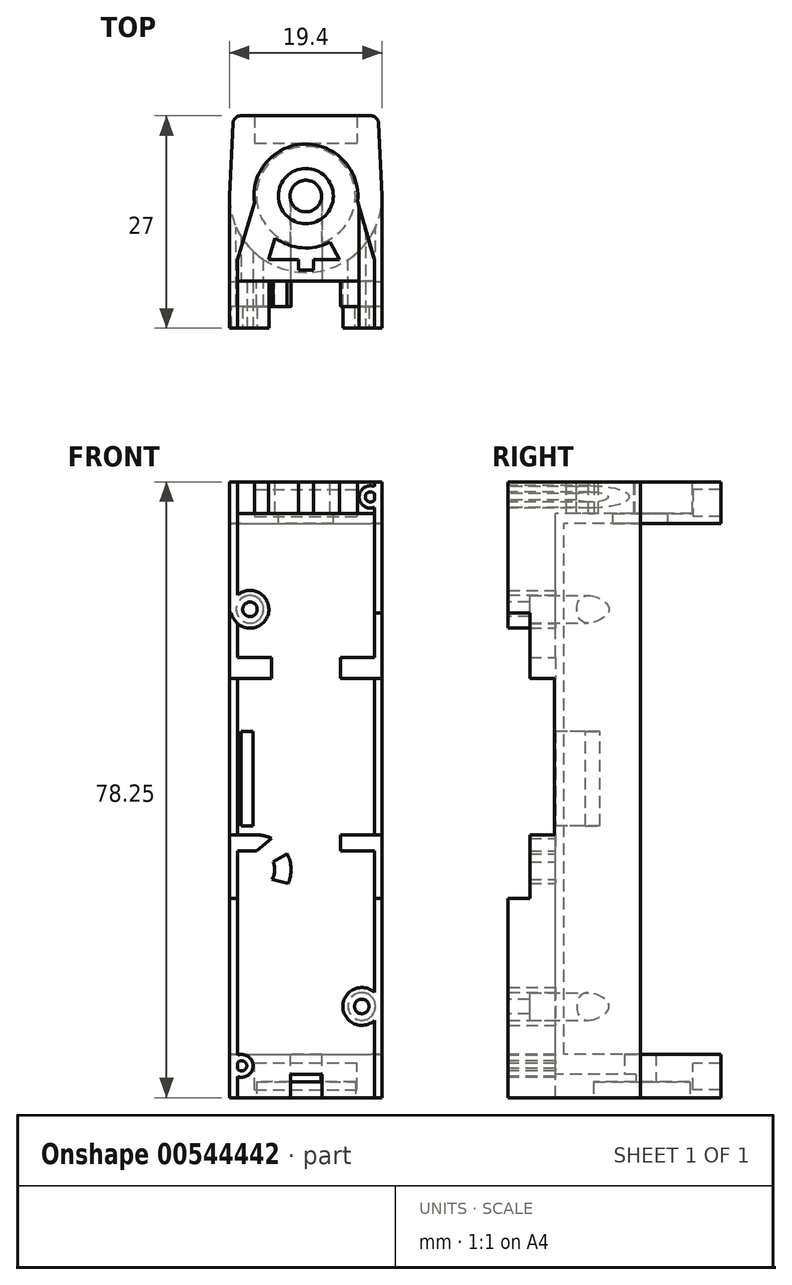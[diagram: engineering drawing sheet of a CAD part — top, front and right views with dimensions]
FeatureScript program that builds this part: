
annotation { "Feature Type Name" : "Feature", "Feature Type Description" : "" }
export const myFeature = defineFeature(function(context is Context, id is Id, definition is map)
    precondition{}
    {
        {
            var Q0;
            Q0=qCreatedBy(makeId("Top.planeOp"),FACE);
            var Q1;
            Q1=qBodyType(qCreatedBy(id+"F3",EDGE),BodyType.WIRE);
            cPlane(context, id + "F0", {"entities" : qUnion([Q0, Q1]), "cplaneType" : CPlaneType.OFFSET, "offset" : 39.25 * mm, "width" : 150 * mm, "height" : 150 * mm});
        }
        {
            var Q0;
            Q0=qCreatedBy(makeId("Front.planeOp"),FACE);
            var sketch = newSketch(context, id + "F1", { "sketchPlane" : qUnion([Q0])});
            skLineSegment(sketch, "E0.bottom", {"start": v(-6.5, 77.25) * mm, "end": v(6.5, 77.25) * mm});
            skLineSegment(sketch, "E0.top", {"start": v(-6.5, 73.85) * mm, "end": v(6.5, 73.85) * mm});
            skLineSegment(sketch, "E0.left", {"start": v(-6.5, 77.25) * mm, "end": v(-6.5, 73.85) * mm});
            skLineSegment(sketch, "E0.right", {"start": v(6.5, 77.25) * mm, "end": v(6.5, 73.85) * mm});
            skLineSegment(sketch, "E1", {"start": v(0, 86.44) * mm, "end": v(0, 62.95) * mm, "construction": true});
            skLineSegment(sketch, "E2.bottom", {"start": v(-6.5, 1) * mm, "end": v(6.5, 1) * mm});
            skLineSegment(sketch, "E2.top", {"start": v(6.5, 4.4) * mm, "end": v(-6.5, 4.4) * mm});
            skLineSegment(sketch, "E2.left", {"start": v(6.5, 1) * mm, "end": v(6.5, 4.4) * mm});
            skLineSegment(sketch, "E2.right", {"start": v(-6.5, 1) * mm, "end": v(-6.5, 4.4) * mm});
            skLineSegment(sketch, "E3", {"start": v(0, 62.95) * mm, "end": v(0, -6.04) * mm, "construction": true});
            skPoint(sketch, "E4", {"position": v(0, 1) * mm});
            skPoint(sketch, "E5", {"position": v(0, 77.25) * mm});
            skLineSegment(sketch, "E6.bottom", {"start": v(-9.7, 78.25) * mm, "end": v(9.7, 78.25) * mm});
            skLineSegment(sketch, "E6.top", {"start": v(-9.7, 72.85) * mm, "end": v(9.7, 72.85) * mm});
            skLineSegment(sketch, "E6.left", {"start": v(-9.7, 78.25) * mm, "end": v(-9.7, 72.85) * mm});
            skLineSegment(sketch, "E6.right", {"start": v(9.7, 78.25) * mm, "end": v(9.7, 72.85) * mm});
            skPoint(sketch, "E7", {"position": v(0, 78.25) * mm});
            skLineSegment(sketch, "E8.top", {"start": v(-9.7, 5.4) * mm, "end": v(9.7, 5.4) * mm});
            skLineSegment(sketch, "E8.left", {"start": v(-9.7, 72.85) * mm, "end": v(-9.7, 5.4) * mm});
            skLineSegment(sketch, "E8.right", {"start": v(9.7, 72.85) * mm, "end": v(9.7, 5.4) * mm});
            skPoint(sketch, "E9", {"position": v(0, 72.85) * mm});
            skLineSegment(sketch, "E10.top", {"start": v(-9.7, 0) * mm, "end": v(9.7, 0) * mm});
            skLineSegment(sketch, "E10.left", {"start": v(-9.7, 5.4) * mm, "end": v(-9.7, 0) * mm});
            skLineSegment(sketch, "E10.right", {"start": v(9.7, 5.4) * mm, "end": v(9.7, 0) * mm});
            skPoint(sketch, "E11", {"position": v(0, 5.4) * mm});
            skPoint(sketch, "E12", {"position": v(0, 0) * mm});
            skLineSegment(sketch, "E13", {"start": v(4.7, 5.4) * mm, "end": v(4.7, 14) * mm, "construction": true});
            skLineSegment(sketch, "E14", {"start": v(4.7, 14) * mm, "end": v(9.7, 14) * mm, "construction": true});
            skCircle(sketch, "E15", {"center": v(7.1, 11.6) * mm, "radius": 2.4 * mm});
            skLineSegment(sketch, "E16", {"start": v(-4.7, 72.85) * mm, "end": v(-4.7, 59.65) * mm, "construction": true});
            skLineSegment(sketch, "E17", {"start": v(-4.7, 59.65) * mm, "end": v(-9.7, 59.65) * mm, "construction": true});
            skCircle(sketch, "E18", {"center": v(-7.1, 62.05) * mm, "radius": 2.4 * mm});
            skCircle(sketch, "E19", {"center": v(-7.1, 62.05) * mm, "radius": 1.75 * mm});
            skCircle(sketch, "E20", {"center": v(7.1, 11.6) * mm, "radius": 1.75 * mm});
            skSolve(sketch);
        }
        {
            var Q0;
            Q0=makeQuery(id+"F1.imprint","IMPRINT",FACE,{"disambiguationData":[TD([[makeQuery(id+"F1.imprint","IMPRINT",EDGE,{"derivedFrom":sQuery(id+"F1.wireOp",EDGE,"E0.bottom")}),1.0]])]});
            var Q1;
            {var subQ4=sQuery(id+"F1.wireOp",EDGE,"E6.top");Q1=makeQuery(id+"F1.imprint","IMPRINT",FACE,{"disambiguationData":[TD([[makeQuery(id+"F1.imprint","IMPRINT",EDGE,{"derivedFrom":subQ4}),-1.0]])]});}
            var Q2;
            Q2=makeQuery(id+"F1.imprint","IMPRINT",FACE,{"disambiguationData":[TD([[makeQuery(id+"F1.imprint","IMPRINT",EDGE,{"derivedFrom":sQuery(id+"F1.wireOp",EDGE,"E18")}),1.0]])]});
            var Q3;
            Q3=makeQuery(id+"F1.imprint","IMPRINT",FACE,{"disambiguationData":[TD([[makeQuery(id+"F1.imprint","IMPRINT",EDGE,{"derivedFrom":sQuery(id+"F1.wireOp",EDGE,"E15")}),1.0]])]});
            var Q4;
            Q4=makeQuery(id+"F1.imprint","IMPRINT",FACE,{"disambiguationData":[TD([[makeQuery(id+"F1.imprint","IMPRINT",EDGE,{"derivedFrom":sQuery(id+"F1.wireOp",EDGE,"E2.bottom")}),-1.0]])]});
            var Q5;
            Q5=makeQuery(id+"F1.imprint","IMPRINT",FACE,{"disambiguationData":[TD([[makeQuery(id+"F1.imprint","IMPRINT",EDGE,{"derivedFrom":sQuery(id+"F1.wireOp",EDGE,"E2.bottom")}),1.0]])]});
            var Q6;
            Q6=makeQuery(id+"F1.imprint","IMPRINT",FACE,{"disambiguationData":[TD([[makeQuery(id+"F1.imprint","IMPRINT",EDGE,{"derivedFrom":sQuery(id+"F1.wireOp",EDGE,"E0.bottom")}),-1.0]])]});
            extrude(context, id + "F2", {"entities" : qUnion([Q0, Q1, Q2, Q3, Q4, Q5, Q6]), "endBound" : BoundingType.SYMMETRIC, "depth" : 27 * mm, "hasSecondDirection" : true, "secondDirectionOppositeDirection" : true, "secondDirectionDepth" : 10.2 * mm});
        }
        {
            var Q0;
            Q0=qCreatedBy(id+"F0.planeOp",FACE);
            var sketch = newSketch(context, id + "F3", { "sketchPlane" : qUnion([Q0])});
            skPoint(sketch, "E21", {"position": v(0, 0) * mm});
            skLineSegment(sketch, "E22.bottom", {"start": v(-9.7, 3.3) * mm, "end": v(9.7, 3.3) * mm});
            skLineSegment(sketch, "E22.top", {"start": v(-9.7, -6.9) * mm, "end": v(9.7, -6.9) * mm});
            skLineSegment(sketch, "E22.left", {"start": v(-9.7, 3.3) * mm, "end": v(-9.7, -6.9) * mm});
            skLineSegment(sketch, "E22.right", {"start": v(9.7, 3.3) * mm, "end": v(9.7, -6.9) * mm});
            skCircle(sketch, "E23", {"center": v(0, 3.3) * mm, "radius": 9.7 * mm});
            skLineSegment(sketch, "E24", {"start": v(0, 3.3) * mm, "end": v(0, -13.5) * mm, "construction": true});
            skLineSegment(sketch, "E25.bottom", {"start": v(-9.7, 13.5) * mm, "end": v(9.7, 13.5) * mm});
            skLineSegment(sketch, "E25.left", {"start": v(-9.7, 13.5) * mm, "end": v(-9.7, 3.3) * mm});
            skLineSegment(sketch, "E25.right", {"start": v(9.7, 13.5) * mm, "end": v(9.7, 3.3) * mm});
            skSolve(sketch);
        }
        {
            var Q0;
            Q0=makeQuery(id+"F1.imprint","IMPRINT",FACE,{"disambiguationData":[TD([[makeQuery(id+"F1.imprint","IMPRINT",EDGE,{"derivedFrom":sQuery(id+"F1.wireOp",EDGE,"E2.bottom")}),1.0]])]});
            var Q1;
            Q1=makeQuery(id+"F1.imprint","IMPRINT",FACE,{"disambiguationData":[TD([[makeQuery(id+"F1.imprint","IMPRINT",EDGE,{"derivedFrom":sQuery(id+"F1.wireOp",EDGE,"E0.bottom")}),-1.0]])]});
            extrude(context, id + "F4", {"entities" : qUnion([Q0, Q1]), "operationType" : NewBodyOperationType.REMOVE, "oppositeDirection" : true, "depth" : 27 * mm, "hasSecondDirection" : true, "secondDirectionOppositeDirection" : true, "secondDirectionDepth" : 10 * mm});
        }
        {
            var Q0;
            {var subQ0=sQuery(id+"F1.wireOp",EDGE,"E10.left");var subQ1=sQuery(id+"F1.wireOp",EDGE,"E8.left");var subQ2=sQuery(id+"F1.wireOp",EDGE,"E6.left");var subQ3=sQuery(id+"F1.wireOp",EDGE,"E10.right");var subQ4=sQuery(id+"F1.wireOp",EDGE,"E8.right");var subQ5=sQuery(id+"F1.wireOp",EDGE,"E6.right");var subQ6=sQuery(id+"F1.wireOp",EDGE,"E10.top");Q0=makeQuery(id+"F31.boolean.opBoolean","SPLIT",FACE,{"disambiguationData":[TD([makeQuery(id+"F2.opExtrude","SWEPT_FACE",FACE,{"disambiguationData":[OSD([subQ6])]})])],"derivedFrom":makeQuery(id+"F2.opExtrude","CAP_FACE",FACE,{"disambiguationData":[OSD([sQuery(id+"F1.wireOp",EDGE,"E6.bottom"),subQ2,subQ5,subQ1,subQ4,subQ6,subQ0,subQ3])],"isStart":true})});}
            var sketch = newSketch(context, id + "F5", { "sketchPlane" : qUnion([Q0])});
            skLineSegment(sketch, "E26.bottom", {"start": v(-6.5, 77.25) * mm, "end": v(6.5, 77.25) * mm});
            skLineSegment(sketch, "E26.top", {"start": v(-6.5, 73.85) * mm, "end": v(6.5, 73.85) * mm});
            skLineSegment(sketch, "E26.left", {"start": v(-6.5, 77.25) * mm, "end": v(-6.5, 73.85) * mm});
            skLineSegment(sketch, "E26.right", {"start": v(6.5, 77.25) * mm, "end": v(6.5, 73.85) * mm});
            skLineSegment(sketch, "E27.bottom", {"start": v(-6.5, 4.4) * mm, "end": v(6.5, 4.4) * mm});
            skLineSegment(sketch, "E27.top", {"start": v(-6.5, 1) * mm, "end": v(6.5, 1) * mm});
            skLineSegment(sketch, "E27.left", {"start": v(-6.5, 4.4) * mm, "end": v(-6.5, 1) * mm});
            skLineSegment(sketch, "E27.right", {"start": v(6.5, 4.4) * mm, "end": v(6.5, 1) * mm});
            skSolve(sketch);
        }
        {
            var Q0;
            Q0=qSketchRegion(id+"F5",true);
            extrude(context, id + "F6", {"entities" : qUnion([Q0]), "operationType" : NewBodyOperationType.ADD, "oppositeDirection" : true, "depth" : 2.1 * mm});
        }
        {
            var Q0;
            Q0=qSketchRegion(id+"F5",true);
            extrude(context, id + "F7", {"entities" : qUnion([Q0]), "operationType" : NewBodyOperationType.REMOVE, "oppositeDirection" : true, "depth" : 2.25 * mm});
        }
        {
            var Q0;
            Q0=makeQuery(id+"F2.opExtrude","SWEPT_FACE",FACE,{"disambiguationData":[OSD([sQuery(id+"F1.wireOp",EDGE,"E6.bottom")])]});
            var sketch = newSketch(context, id + "F8", { "sketchPlane" : qUnion([Q0])});
            skCircle(sketch, "E28", {"center": v(0, 3.3) * mm, "radius": 3.5 * mm});
            skSolve(sketch);
        }
        {
            var Q0;
            Q0=qSketchRegion(id+"F8",true);
            extrude(context, id + "F9", {"entities" : qUnion([Q0]), "operationType" : NewBodyOperationType.REMOVE, "endBound" : BoundingType.SYMMETRIC, "oppositeDirection" : true, "depth" : 15 * mm});
        }
        {
            var Q0;
            Q0=makeQuery(id+"F2.opExtrude","SWEPT_FACE",FACE,{"disambiguationData":[OSD([sQuery(id+"F1.wireOp",EDGE,"E10.top")])]});
            var sketch = newSketch(context, id + "F10", { "sketchPlane" : qUnion([Q0])});
            skCircle(sketch, "E29", {"center": v(0, -3.3) * mm, "radius": 2 * mm});
            skSolve(sketch);
        }
        {
            var Q0;
            Q0=qSketchRegion(id+"F10",true);
            extrude(context, id + "F11", {"entities" : qUnion([Q0]), "operationType" : NewBodyOperationType.REMOVE, "endBound" : BoundingType.SYMMETRIC, "oppositeDirection" : true, "depth" : 15 * mm});
        }
        {
            var Q0;
            Q0=makeQuery(id+"F2.opExtrude","SWEPT_FACE",FACE,{"disambiguationData":[OSD([sQuery(id+"F1.wireOp",EDGE,"E6.bottom")])]});
            var sketch = newSketch(context, id + "F12", { "sketchPlane" : qUnion([Q0])});
            skLineSegment(sketch, "E30", {"start": v(2.97, -4.05) * mm, "end": v(2.97, -4.05) * mm});
            skLineSegment(sketch, "E31", {"start": v(-4.57, -5.74) * mm, "end": v(-4.57, -5.74) * mm});
            skLineSegment(sketch, "E32", {"start": v(-9.7, -4.8) * mm, "end": v(-8.7, -4.8) * mm});
            skCircle(sketch, "E33", {"center": v(0, 3.3) * mm, "radius": 6.6 * mm});
            skLineSegment(sketch, "E34.bottom", {"start": v(-0.95, -3.8) * mm, "end": v(0.95, -3.8) * mm});
            skLineSegment(sketch, "E34.top", {"start": v(-0.95, -6.1) * mm, "end": v(0.95, -6.1) * mm});
            skLineSegment(sketch, "E34.left", {"start": v(-0.95, -3.8) * mm, "end": v(-0.95, -6.1) * mm});
            skLineSegment(sketch, "E34.right", {"start": v(0.95, -3.8) * mm, "end": v(0.95, -6.1) * mm});
            skLineSegment(sketch, "E35", {"start": v(-3.9, -2.02) * mm, "end": v(-4.73, -4.8) * mm});
            skLineSegment(sketch, "E36", {"start": v(-6.54, 2.45) * mm, "end": v(-8.7, -4.8) * mm});
            skLineSegment(sketch, "E37", {"start": v(6.57, 2.63) * mm, "end": v(8.7, -4.8) * mm});
            skLineSegment(sketch, "E38", {"start": v(3.05, -2.55) * mm, "end": v(4.27, -4.8) * mm});
            skLineSegment(sketch, "E39", {"start": v(-8.7, -4.8) * mm, "end": v(-8.7, -13.5) * mm});
            skLineSegment(sketch, "E40", {"start": v(8.7, -4.8) * mm, "end": v(8.7, -13.5) * mm});
            skLineSegment(sketch, "E41", {"start": v(-8.7, -4.8) * mm, "end": v(-4.73, -4.8) * mm});
            skLineSegment(sketch, "E42", {"start": v(-8.7, -4.8) * mm, "end": v(-8.7, -4.8) * mm});
            skLineSegment(sketch, "E43", {"start": v(-4.73, -4.8) * mm, "end": v(-4.73, -4.8) * mm});
            skLineSegment(sketch, "E44", {"start": v(-4.73, -4.8) * mm, "end": v(4.27, -4.8) * mm});
            skLineSegment(sketch, "E45", {"start": v(4.27, -4.8) * mm, "end": v(4.27, -4.8) * mm});
            skLineSegment(sketch, "E46", {"start": v(4.27, -4.8) * mm, "end": v(8.7, -4.8) * mm});
            skLineSegment(sketch, "E47", {"start": v(8.7, -4.8) * mm, "end": v(8.7, -4.8) * mm});
            skLineSegment(sketch, "E48", {"start": v(9.67, -4.8) * mm, "end": v(9.7, -4.8) * mm});
            skLineSegment(sketch, "E49", {"start": v(8.7, -4.8) * mm, "end": v(9.67, -4.8) * mm});
            skLineSegment(sketch, "E50", {"start": v(-8.7, -13.5) * mm, "end": v(8.7, -13.5) * mm});
            skLineSegment(sketch, "E51", {"start": v(-8.7, -7.5) * mm, "end": v(8.7, -7.5) * mm});
            skSolve(sketch);
        }
        {
            var Q0;
            {var subQ0=sQuery(id+"F12.wireOp",EDGE,"E35");Q0=makeQuery(id+"F12.imprint","IMPRINT",FACE,{"disambiguationData":[TD([[makeQuery(id+"F12.imprint","IMPRINT",EDGE,{"derivedFrom":subQ0}),-1.0]])]});}
            var Q1;
            {var subQ0=sQuery(id+"F12.wireOp",EDGE,"E37");Q1=makeQuery(id+"F12.imprint","IMPRINT",FACE,{"disambiguationData":[TD([[makeQuery(id+"F12.imprint","IMPRINT",EDGE,{"derivedFrom":subQ0}),-1.0]])]});}
            var Q2;
            {var subQ1=sQuery(id+"F12.wireOp",EDGE,"E34.top");Q2=makeQuery(id+"F12.imprint","IMPRINT",FACE,{"disambiguationData":[TD([[makeQuery(id+"F12.imprint","IMPRINT",EDGE,{"derivedFrom":subQ1}),-1.0]])]});}
            var Q3;
            Q3=makeQuery(id+"F12.imprint","IMPRINT",FACE,{"disambiguationData":[TD([[makeQuery(id+"F12.imprint","IMPRINT",EDGE,{"derivedFrom":makeQuery(id+"F9.boolean.opBoolean","INTERSECT",EDGE,{"derivedFrom":[makeQuery(id+"F2.opExtrude","SWEPT_FACE",FACE,{"disambiguationData":[OSD([sQuery(id+"F1.wireOp",EDGE,"E6.bottom")])]}),makeQuery(id+"F9.opExtrude","SWEPT_FACE",FACE,{"disambiguationData":[OSD([sQuery(id+"F8.wireOp",EDGE,"E28")])]})]})}),-1.0]])]});
            extrude(context, id + "F13", {"entities" : qUnion([Q0, Q1, Q2, Q3]), "operationType" : NewBodyOperationType.REMOVE, "oppositeDirection" : true, "depth" : 4 * mm});
        }
        {
            var Q0;
            {var subQ0=sQuery(id+"F12.wireOp",EDGE,"E50");Q0=makeQuery(id+"F12.imprint","IMPRINT",FACE,{"disambiguationData":[TD([[makeQuery(id+"F12.imprint","IMPRINT",EDGE,{"derivedFrom":subQ0}),1.0]])]});}
            extrude(context, id + "F14", {"entities" : qUnion([Q0]), "operationType" : NewBodyOperationType.REMOVE, "oppositeDirection" : true, "depth" : 80 * mm});
        }
        {
            var Q0;
            Q0=makeQuery(id+"F2.opExtrude","SWEPT_FACE",FACE,{"disambiguationData":[OSD([sQuery(id+"F1.wireOp",EDGE,"E10.top")])]});
            var sketch = newSketch(context, id + "F15", { "sketchPlane" : qUnion([Q0])});
            skLineSegment(sketch, "E52.bottom", {"start": v(-1.92, -2.75) * mm, "end": v(2.07, -2.75) * mm});
            skLineSegment(sketch, "E52.top", {"start": v(-1.92, 8.64) * mm, "end": v(2.07, 8.64) * mm});
            skLineSegment(sketch, "E52.left", {"start": v(-1.92, -2.75) * mm, "end": v(-1.92, 8.64) * mm});
            skLineSegment(sketch, "E52.right", {"start": v(2.07, -2.75) * mm, "end": v(2.07, 8.64) * mm});
            skSolve(sketch);
        }
        {
            var Q0;
            {var subQ0=sQuery(id+"F15.wireOp",EDGE,"E52.top");Q0=makeQuery(id+"F15.imprint","IMPRINT",FACE,{"disambiguationData":[TD([[makeQuery(id+"F15.imprint","IMPRINT",EDGE,{"derivedFrom":subQ0}),-1.0]])]});}
            var Q1;
            {var subQ0=sQuery(id+"F15.wireOp",EDGE,"E52.bottom");Q1=makeQuery(id+"F15.imprint","IMPRINT",FACE,{"disambiguationData":[TD([[makeQuery(id+"F15.imprint","IMPRINT",EDGE,{"derivedFrom":subQ0}),1.0]])]});}
            var Q2;
            {var subQ1=makeQuery(id+"F2.opExtrude","SWEPT_FACE",FACE,{"disambiguationData":[OSD([sQuery(id+"F1.wireOp",EDGE,"E10.top")])]});var subQ4=makeQuery(id+"F14.boolean.opBoolean","INTERSECT",EDGE,{"derivedFrom":[subQ1,makeQuery(id+"F14.opExtrude","SWEPT_FACE",FACE,{"disambiguationData":[OSD([sQuery(id+"F12.wireOp",EDGE,"E51")])]})]});var subQ6=sQuery(id+"F15.wireOp",EDGE,"E52.right");var subQ7=makeQuery(id+"F15.imprint","INTERSECT",VERTEX,{"derivedFrom":[subQ4,subQ6]});Q2=makeQuery(id+"F15.imprint","IMPRINT",FACE,{"disambiguationData":[TD([[makeQuery(id+"F15.imprint","IMPRINT",EDGE,{"disambiguationData":[TD([[subQ7,1.0]])],"derivedFrom":subQ6}),1.0]])]});}
            extrude(context, id + "F16", {"entities" : qUnion([Q0, Q1, Q2]), "operationType" : NewBodyOperationType.REMOVE, "oppositeDirection" : true, "depth" : 3 * mm});
        }
        {
            var Q0;
            Q0=makeQuery(id+"F2.opExtrude","SWEPT_FACE",FACE,{"disambiguationData":[OSD([sQuery(id+"F1.wireOp",EDGE,"E6.left"),sQuery(id+"F1.wireOp",EDGE,"E8.left"),sQuery(id+"F1.wireOp",EDGE,"E10.left")])]});
            var sketch = newSketch(context, id + "F17", { "sketchPlane" : qUnion([Q0])});
            skLineSegment(sketch, "E53.bottom", {"start": v(14.36, 61.6) * mm, "end": v(10.74, 61.6) * mm});
            skLineSegment(sketch, "E53.top", {"start": v(14.36, 25.3) * mm, "end": v(10.74, 25.3) * mm});
            skLineSegment(sketch, "E53.left", {"start": v(14.36, 61.6) * mm, "end": v(14.36, 25.3) * mm});
            skLineSegment(sketch, "E53.right", {"start": v(10.74, 61.6) * mm, "end": v(10.74, 25.3) * mm});
            skLineSegment(sketch, "E54.bottom", {"start": v(7.6, 53.25) * mm, "end": v(20.25, 53.25) * mm});
            skLineSegment(sketch, "E54.top", {"start": v(7.6, 33.4) * mm, "end": v(20.25, 33.4) * mm});
            skLineSegment(sketch, "E54.left", {"start": v(7.6, 53.25) * mm, "end": v(7.6, 33.4) * mm});
            skLineSegment(sketch, "E54.right", {"start": v(20.25, 53.25) * mm, "end": v(20.25, 33.4) * mm});
            skSolve(sketch);
        }
        {
            var Q0;
            {var subQ0=sQuery(id+"F17.wireOp",EDGE,"E54.bottom");var subQ1=sQuery(id+"F17.wireOp",EDGE,"E53.right");var subQ2=makeQuery(id+"F17.imprint","INTERSECT",VERTEX,{"derivedFrom":[subQ1,subQ0]});Q0=makeQuery(id+"F17.imprint","IMPRINT",FACE,{"disambiguationData":[TD([[makeQuery(id+"F17.imprint","IMPRINT",EDGE,{"disambiguationData":[TD([[subQ2,-1.0]])],"derivedFrom":subQ1}),1.0]])]});}
            var Q1;
            {var subQ0=sQuery(id+"F17.wireOp",EDGE,"E53.right");var subQ1=sQuery(id+"F17.wireOp",EDGE,"E53.bottom");var subQ2=makeQuery(id+"F17.imprint","INTERSECT",VERTEX,{"derivedFrom":[subQ1,subQ0]});Q1=makeQuery(id+"F17.imprint","IMPRINT",FACE,{"disambiguationData":[TD([[makeQuery(id+"F17.imprint","IMPRINT",EDGE,{"disambiguationData":[TD([[subQ2,-1.0]])],"derivedFrom":subQ0}),1.0]])]});}
            var Q2;
            {var subQ5=sQuery(id+"F17.wireOp",EDGE,"E54.left");Q2=makeQuery(id+"F17.imprint","IMPRINT",FACE,{"disambiguationData":[TD([[makeQuery(id+"F17.imprint","IMPRINT",EDGE,{"derivedFrom":subQ5}),1.0]])]});}
            var Q3;
            {var subQ0=sQuery(id+"F17.wireOp",EDGE,"E53.right");var subQ1=sQuery(id+"F17.wireOp",EDGE,"E53.top");var subQ2=makeQuery(id+"F17.imprint","INTERSECT",VERTEX,{"derivedFrom":[subQ1,subQ0]});Q3=makeQuery(id+"F17.imprint","IMPRINT",FACE,{"disambiguationData":[TD([[makeQuery(id+"F17.imprint","IMPRINT",EDGE,{"disambiguationData":[TD([[subQ2,1.0]])],"derivedFrom":subQ0}),1.0]])]});}
            extrude(context, id + "F18", {"entities" : qUnion([Q0, Q1, Q2, Q3]), "operationType" : NewBodyOperationType.REMOVE, "endBound" : BoundingType.SYMMETRIC, "oppositeDirection" : true, "depth" : 40 * mm});
        }
        {
            var Q0;
            Q0=makeQuery(id+"F2.opExtrude","SWEPT_FACE",FACE,{"disambiguationData":[OSD([sQuery(id+"F1.wireOp",EDGE,"E6.left"),sQuery(id+"F1.wireOp",EDGE,"E8.left"),sQuery(id+"F1.wireOp",EDGE,"E10.left")])]});
            var sketch = newSketch(context, id + "F19", { "sketchPlane" : qUnion([Q0])});
            skLineSegment(sketch, "E55.bottom", {"start": v(7.6, 53.25) * mm, "end": v(10.74, 53.25) * mm});
            skLineSegment(sketch, "E55.top", {"start": v(6.6, 55.96) * mm, "end": v(10.74, 55.96) * mm});
            skLineSegment(sketch, "E55.left", {"start": v(6.6, 53.25) * mm, "end": v(6.6, 55.96) * mm});
            skLineSegment(sketch, "E55.right", {"start": v(10.74, 53.25) * mm, "end": v(10.74, 55.96) * mm});
            skLineSegment(sketch, "E56.bottom", {"start": v(7.6, 33.4) * mm, "end": v(10.74, 33.4) * mm});
            skLineSegment(sketch, "E56.top", {"start": v(7.6, 31.33) * mm, "end": v(10.74, 31.33) * mm});
            skLineSegment(sketch, "E56.left", {"start": v(7.6, 33.4) * mm, "end": v(7.6, 31.33) * mm});
            skLineSegment(sketch, "E56.right", {"start": v(10.74, 33.4) * mm, "end": v(10.74, 31.33) * mm});
            skLineSegment(sketch, "E57", {"start": v(6.6, 53.25) * mm, "end": v(7.6, 53.25) * mm});
            skLineSegment(sketch, "E58", {"start": v(7.6, 31.33) * mm, "end": v(6.6, 31.33) * mm});
            skLineSegment(sketch, "E59", {"start": v(6.6, 31.33) * mm, "end": v(6.6, 33.4) * mm});
            skLineSegment(sketch, "E60", {"start": v(6.6, 33.4) * mm, "end": v(7.6, 33.4) * mm});
            skSolve(sketch);
        }
        {
            var Q0;
            Q0=makeQuery(id+"F19.imprint","IMPRINT",FACE,{"disambiguationData":[TD([[makeQuery(id+"F19.imprint","IMPRINT",EDGE,{"derivedFrom":sQuery(id+"F19.wireOp",EDGE,"E55.bottom")}),-1.0]])]});
            var Q1;
            Q1=makeQuery(id+"F19.imprint","IMPRINT",FACE,{"disambiguationData":[TD([[makeQuery(id+"F19.imprint","IMPRINT",EDGE,{"derivedFrom":sQuery(id+"F19.wireOp",EDGE,"E56.left")}),-1.0]])]});
            var Q2;
            Q2=makeQuery(id+"F19.imprint","IMPRINT",FACE,{"disambiguationData":[TD([[makeQuery(id+"F19.imprint","IMPRINT",EDGE,{"derivedFrom":sQuery(id+"F19.wireOp",EDGE,"E56.bottom")}),1.0]])]});
            var Q3;
            {var subQ0=sQuery(id+"F12.wireOp",EDGE,"E40");Q3=makeQuery(id+"F14.boolean.opBoolean","MERGE",FACE,{"derivedFrom":[makeQuery(id+"F13.boolean.opBoolean","COPY",FACE,{"derivedFrom":makeQuery(id+"F13.opExtrude","SWEPT_FACE",FACE,{"disambiguationData":[OSD([subQ0])]})}),makeQuery(id+"F14.opExtrude","SWEPT_FACE",FACE,{"disambiguationData":[OSD([subQ0])]})]});}
            extrude(context, id + "F20", {"entities" : qUnion([Q0, Q1, Q2]), "operationType" : NewBodyOperationType.ADD, "endBound" : BoundingType.UP_TO_SURFACE, "oppositeDirection" : true, "endBoundEntityFace" : qUnion([Q3]), "depth" : 25 * mm});
        }
        {
            var Q0;
            Q0=makeQuery(id+"F1.imprint","IMPRINT",FACE,{"disambiguationData":[TD([[makeQuery(id+"F1.imprint","IMPRINT",EDGE,{"derivedFrom":sQuery(id+"F1.wireOp",EDGE,"E19")}),1.0]])]});
            extrude(context, id + "F21", {"entities" : qUnion([Q0]), "operationType" : NewBodyOperationType.REMOVE, "depth" : 25 * mm});
        }
        {
            var Q0;
            Q0=makeQuery(id+"F1.imprint","IMPRINT",FACE,{"disambiguationData":[TD([[makeQuery(id+"F1.imprint","IMPRINT",EDGE,{"derivedFrom":sQuery(id+"F1.wireOp",EDGE,"E15")}),1.0]])]});
            var Q1;
            Q1=makeQuery(id+"F1.imprint","IMPRINT",FACE,{"disambiguationData":[TD([[makeQuery(id+"F1.imprint","IMPRINT",EDGE,{"derivedFrom":sQuery(id+"F1.wireOp",EDGE,"E18")}),1.0]])]});
            var Q2;
            Q2=sQuery(id+"F1.wireOp",EDGE,"E15");
            var Q3;
            Q3=sQuery(id+"F1.wireOp",EDGE,"E20");
            var Q4;
            {var subQ2=sQuery(id+"F1.wireOp",EDGE,"E10.top");var subQ3=makeQuery(id+"F2.opExtrude","SWEPT_FACE",FACE,{"disambiguationData":[OSD([subQ2])]});var subQ4=sQuery(id+"F1.wireOp",EDGE,"E20");var subQ5=makeQuery(id+"F2.opExtrude","SWEPT_FACE",FACE,{"disambiguationData":[OSD([subQ4])]});var subQ6=sQuery(id+"F1.wireOp",EDGE,"E10.right");var subQ7=sQuery(id+"F1.wireOp",EDGE,"E8.right");var subQ8=sQuery(id+"F1.wireOp",EDGE,"E6.right");var subQ11=sQuery(id+"F1.wireOp",EDGE,"E6.bottom");Q4=makeQuery(id+"F18.boolean.opBoolean","SPLIT",FACE,{"disambiguationData":[TD([subQ3])],"derivedFrom":makeQuery(id+"F14.boolean.opBoolean","SPLIT",FACE,{"disambiguationData":[TD([subQ5])],"derivedFrom":makeQuery(id+"F2.opExtrude","CAP_FACE",FACE,{"disambiguationData":[OSD([subQ11,sQuery(id+"F1.wireOp",EDGE,"E6.left"),subQ8,sQuery(id+"F1.wireOp",EDGE,"E8.left"),subQ7,subQ2,sQuery(id+"F1.wireOp",EDGE,"E10.left"),subQ6,sQuery(id+"F1.wireOp",EDGE,"E19"),subQ4])],"isStart":false})})});}
            extrude(context, id + "F22", {"entities" : qUnion([Q0, Q1]), "operationType" : NewBodyOperationType.ADD, "surfaceEntities" : qUnion([Q2, Q3]), "endBound" : BoundingType.UP_TO_SURFACE, "endBoundEntityFace" : qUnion([Q4]), "depth" : 25 * mm});
        }
        {
            var Q0;
            Q0=makeQuery(id+"F2.opExtrude","SWEPT_FACE",FACE,{"disambiguationData":[OSD([sQuery(id+"F1.wireOp",EDGE,"E10.top")])]});
            var sketch = newSketch(context, id + "F23", { "sketchPlane" : qUnion([Q0])});
            skLineSegment(sketch, "E61", {"start": v(-4.38, 7.5) * mm, "end": v(-4.38, 10.76) * mm});
            skLineSegment(sketch, "E62", {"start": v(-4.38, 10.76) * mm, "end": v(4.42, 10.76) * mm});
            skLineSegment(sketch, "E63", {"start": v(4.42, 10.76) * mm, "end": v(4.42, 7.5) * mm});
            skLineSegment(sketch, "E64", {"start": v(4.42, 7.5) * mm, "end": v(-4.38, 7.5) * mm});
            skSolve(sketch);
        }
        {
            var Q0;
            Q0=qSketchRegion(id+"F23",true);
            extrude(context, id + "F24", {"entities" : qUnion([Q0]), "operationType" : NewBodyOperationType.REMOVE, "oppositeDirection" : true, "depth" : 80 * mm});
        }
        {
            var Q0;
            {var subQ8=sQuery(id+"F12.wireOp",EDGE,"E51");var subQ9=makeQuery(id+"F14.boolean.opBoolean","COPY",FACE,{"derivedFrom":makeQuery(id+"F14.opExtrude","SWEPT_FACE",FACE,{"disambiguationData":[OSD([subQ8])]})});Q0=makeQuery(id+"F24.boolean.opBoolean","MERGE",FACE,{"derivedFrom":[makeQuery(id+"F20.boolean.opBoolean","SPLIT",FACE,{"disambiguationData":[TD([makeQuery(id+"F20.opExtrude","SWEPT_FACE",FACE,{"disambiguationData":[OSD([sQuery(id+"F19.wireOp",EDGE,"E55.bottom"),sQuery(id+"F19.wireOp",EDGE,"E57")])]})])],"derivedFrom":subQ9}),makeQuery(id+"F20.boolean.opBoolean","SPLIT",FACE,{"disambiguationData":[TD([makeQuery(id+"F20.opExtrude","SWEPT_FACE",FACE,{"disambiguationData":[OSD([sQuery(id+"F19.wireOp",EDGE,"E55.top")])]})])],"derivedFrom":subQ9}),makeQuery(id+"F20.boolean.opBoolean","SPLIT",FACE,{"disambiguationData":[TD([makeQuery(id+"F2.opExtrude","SWEPT_FACE",FACE,{"disambiguationData":[OSD([sQuery(id+"F1.wireOp",EDGE,"E10.top")])]})])],"derivedFrom":subQ9}),makeQuery(id+"F24.opExtrude","SWEPT_FACE",FACE,{"disambiguationData":[OSD([sQuery(id+"F23.wireOp",EDGE,"E64")])]})]});}
            var sketch = newSketch(context, id + "F25", { "sketchPlane" : qUnion([Q0])});
            skCircle(sketch, "E65", {"center": v(8.2, 76.33) * mm, "radius": 1.43 * mm});
            skCircle(sketch, "E66", {"center": v(8.2, 76.33) * mm, "radius": 0.65 * mm});
            skCircle(sketch, "E67", {"center": v(-8.15, 4.05) * mm, "radius": 1.45 * mm});
            skCircle(sketch, "E68", {"center": v(-8.15, 4.05) * mm, "radius": 0.65 * mm});
            skLineSegment(sketch, "E69", {"start": v(-13.44, 5.5) * mm, "end": v(16.51, 5.5) * mm, "construction": true});
            skLineSegment(sketch, "E70", {"start": v(-6.7, 11.1) * mm, "end": v(-6.7, -5.63) * mm, "construction": true});
            skSolve(sketch);
        }
        {
            var Q0;
            Q0=qSketchRegion(id+"F25",true);
            var Q1;
            {var subQ0=sQuery(id+"F1.wireOp",EDGE,"E10.left");var subQ1=sQuery(id+"F1.wireOp",EDGE,"E8.left");var subQ2=sQuery(id+"F1.wireOp",EDGE,"E6.left");var subQ3=sQuery(id+"F1.wireOp",EDGE,"E10.right");var subQ4=sQuery(id+"F1.wireOp",EDGE,"E8.right");var subQ5=sQuery(id+"F1.wireOp",EDGE,"E6.right");var subQ6=sQuery(id+"F1.wireOp",EDGE,"E10.top");Q1=makeQuery(id+"F6.boolean.opBoolean","MERGE",FACE,{"derivedFrom":[makeQuery(id+"F31.boolean.opBoolean","SPLIT",FACE,{"disambiguationData":[TD([makeQuery(id+"F2.opExtrude","SWEPT_FACE",FACE,{"disambiguationData":[OSD([subQ6])]})])],"derivedFrom":makeQuery(id+"F2.opExtrude","CAP_FACE",FACE,{"disambiguationData":[OSD([sQuery(id+"F1.wireOp",EDGE,"E6.bottom"),subQ2,subQ5,subQ1,subQ4,subQ6,subQ0,subQ3])],"isStart":true})}),makeQuery(id+"F6.opExtrude","CAP_FACE",FACE,{"disambiguationData":[OSD([sQuery(id+"F5.wireOp",EDGE,"E27.bottom"),sQuery(id+"F5.wireOp",EDGE,"E27.top"),sQuery(id+"F5.wireOp",EDGE,"E27.left"),sQuery(id+"F5.wireOp",EDGE,"E27.right")])],"isStart":true})]});}
            var Q2;
            Q2=sQuery(id+"F1.wireOp",VERTEX,"E7");
            var Q3;
            {var subQ0=sQuery(id+"F12.wireOp",EDGE,"E39");var subQ2=sQuery(id+"F1.wireOp",EDGE,"E10.left");var subQ3=sQuery(id+"F1.wireOp",EDGE,"E8.left");var subQ4=sQuery(id+"F1.wireOp",EDGE,"E6.left");var subQ6=sQuery(id+"F1.wireOp",EDGE,"E10.top");var subQ7=makeQuery(id+"F2.opExtrude","SWEPT_FACE",FACE,{"disambiguationData":[OSD([subQ6])]});var subQ8=makeQuery(id+"F13.boolean.opBoolean","COPY",FACE,{"derivedFrom":makeQuery(id+"F13.opExtrude","SWEPT_FACE",FACE,{"disambiguationData":[OSD([subQ0])]})});var subQ9=sQuery(id+"F1.wireOp",EDGE,"E6.bottom");Q3=makeQuery(id+"F18.boolean.opBoolean","SPLIT",FACE,{"disambiguationData":[TD([subQ7])],"derivedFrom":makeQuery(id+"F14.boolean.opBoolean","SPLIT",FACE,{"disambiguationData":[TD([subQ8])],"derivedFrom":makeQuery(id+"F2.opExtrude","CAP_FACE",FACE,{"disambiguationData":[OSD([subQ9,subQ4,sQuery(id+"F1.wireOp",EDGE,"E6.right"),subQ3,sQuery(id+"F1.wireOp",EDGE,"E8.right"),subQ6,subQ2,sQuery(id+"F1.wireOp",EDGE,"E10.right")])],"isStart":false})})});}
            extrude(context, id + "F26", {"entities" : qUnion([Q0]), "operationType" : NewBodyOperationType.ADD, "endBound" : BoundingType.UP_TO_SURFACE, "oppositeDirection" : true, "endBoundEntityFace" : qUnion([Q1]), "endBoundEntityVertex" : qUnion([Q2]), "depth" : 25 * mm, "hasSecondDirection" : true, "secondDirectionBound" : SecondDirectionBoundingType.UP_TO_SURFACE, "secondDirectionOppositeDirection" : false, "secondDirectionBoundEntityFace" : qUnion([Q3]), "secondDirectionDepth" : 25 * mm});
        }
        {
            var Q0;
            Q0=makeQuery(id+"F22.opExtrude","CAP_FACE",FACE,{"disambiguationData":[OSD([sQuery(id+"F1.wireOp",EDGE,"E18"),sQuery(id+"F1.wireOp",EDGE,"E19")])],"isStart":false});
            var sketch = newSketch(context, id + "F27", { "sketchPlane" : qUnion([Q0])});
            skCircle(sketch, "E71", {"center": v(-7.1, 62.05) * mm, "radius": 0.93 * mm});
            skCircle(sketch, "E72", {"center": v(7.1, 11.6) * mm, "radius": 0.93 * mm});
            skCircle(sketch, "E73", {"center": v(7.1, 11.6) * mm, "radius": 1.87 * mm});
            skSolve(sketch);
        }
        {
            var Q0;
            Q0=makeQuery(id+"F27.imprint","IMPRINT",FACE,{"disambiguationData":[TD([[makeQuery(id+"F27.imprint","IMPRINT",EDGE,{"derivedFrom":sQuery(id+"F27.wireOp",EDGE,"E71")}),-1.0]])]});
            var Q1;
            Q1=makeQuery(id+"F27.imprint","IMPRINT",FACE,{"disambiguationData":[TD([[makeQuery(id+"F27.imprint","IMPRINT",EDGE,{"derivedFrom":sQuery(id+"F27.wireOp",EDGE,"E72")}),-1.0]])]});
            extrude(context, id + "F28", {"entities" : qUnion([Q0, Q1]), "operationType" : NewBodyOperationType.ADD, "oppositeDirection" : true, "depth" : 2.75 * mm});
        }
        {
            var Q0;
            {var subQ1=sQuery(id+"F12.wireOp",EDGE,"E39");var subQ2=makeQuery(id+"F14.opExtrude","SWEPT_FACE",FACE,{"disambiguationData":[OSD([subQ1])]});var subQ3=makeQuery(id+"F14.boolean.opBoolean","COPY",FACE,{"derivedFrom":subQ2});var subQ7=sQuery(id+"F17.wireOp",EDGE,"E54.top");var subQ9=makeQuery(id+"F18.opExtrude","SWEPT_FACE",FACE,{"disambiguationData":[OSD([subQ7])]});var subQ10=makeQuery(id+"F18.boolean.opBoolean","COPY",FACE,{"disambiguationData":[TD([subQ3])],"derivedFrom":subQ9});var subQ11=makeQuery(id+"F24.opExtrude","SWEPT_FACE",FACE,{"disambiguationData":[OSD([sQuery(id+"F23.wireOp",EDGE,"E64")])]});var subQ14=sQuery(id+"F12.wireOp",EDGE,"E40");var subQ15=makeQuery(id+"F14.opExtrude","SWEPT_FACE",FACE,{"disambiguationData":[OSD([subQ14])]});var subQ16=makeQuery(id+"F13.boolean.opBoolean","COPY",FACE,{"derivedFrom":makeQuery(id+"F13.opExtrude","SWEPT_FACE",FACE,{"disambiguationData":[OSD([subQ14])]})});var subQ19=sQuery(id+"F12.wireOp",EDGE,"E51");var subQ20=makeQuery(id+"F14.boolean.opBoolean","COPY",FACE,{"derivedFrom":makeQuery(id+"F14.opExtrude","SWEPT_FACE",FACE,{"disambiguationData":[OSD([subQ19])]})});var subQ21=makeQuery(id+"F18.boolean.opBoolean","COPY",FACE,{"disambiguationData":[TD([subQ16])],"derivedFrom":subQ9});var subQ22=makeQuery(id+"F20.opExtrude","SWEPT_FACE",FACE,{"disambiguationData":[OSD([sQuery(id+"F19.wireOp",EDGE,"E56.bottom"),sQuery(id+"F19.wireOp",EDGE,"E60")])]});var subQ24=makeQuery(id+"F20.opExtrude","SWEPT_FACE",FACE,{"disambiguationData":[OSD([sQuery(id+"F19.wireOp",EDGE,"E56.top"),sQuery(id+"F19.wireOp",EDGE,"E58")])]});var subQ26=makeQuery(id+"F20.opExtrude","SWEPT_FACE",FACE,{"disambiguationData":[OSD([sQuery(id+"F19.wireOp",EDGE,"E55.top")])]});var subQ28=sQuery(id+"F17.wireOp",EDGE,"E54.bottom");var subQ30=makeQuery(id+"F18.opExtrude","SWEPT_FACE",FACE,{"disambiguationData":[OSD([subQ28])]});var subQ31=makeQuery(id+"F18.boolean.opBoolean","COPY",FACE,{"disambiguationData":[TD([subQ3])],"derivedFrom":subQ30});var subQ32=sQuery(id+"F15.wireOp",EDGE,"E52.right");var subQ33=makeQuery(id+"F16.boolean.opBoolean","COPY",FACE,{"derivedFrom":makeQuery(id+"F16.opExtrude","SWEPT_FACE",FACE,{"disambiguationData":[OSD([subQ32])]})});var subQ34=makeQuery(id+"F13.boolean.opBoolean","COPY",FACE,{"derivedFrom":makeQuery(id+"F13.opExtrude","SWEPT_FACE",FACE,{"disambiguationData":[OSD([subQ1])]})});var subQ35=makeQuery(id+"F2.opExtrude","SWEPT_FACE",FACE,{"disambiguationData":[OSD([sQuery(id+"F1.wireOp",EDGE,"E10.top")])]});var subQ36=makeQuery(id+"F14.boolean.opBoolean","COPY",FACE,{"derivedFrom":subQ15});var subQ37=makeQuery(id+"F13.boolean.opBoolean","COPY",FACE,{"derivedFrom":makeQuery(id+"F13.opExtrude","CAP_FACE",FACE,{"disambiguationData":[OSD([sQuery(id+"F1.wireOp",EDGE,"E6.bottom"),sQuery(id+"F8.wireOp",EDGE,"E28"),sQuery(id+"F12.wireOp",EDGE,"E33"),sQuery(id+"F12.wireOp",EDGE,"E34.top"),sQuery(id+"F12.wireOp",EDGE,"E34.left"),sQuery(id+"F12.wireOp",EDGE,"E34.right"),sQuery(id+"F12.wireOp",EDGE,"E35"),sQuery(id+"F12.wireOp",EDGE,"E36"),sQuery(id+"F12.wireOp",EDGE,"E37"),sQuery(id+"F12.wireOp",EDGE,"E38"),subQ1,subQ14,sQuery(id+"F12.wireOp",EDGE,"E44"),subQ19])],"isStart":false})});var subQ38=makeQuery(id+"F20.opExtrude","SWEPT_FACE",FACE,{"disambiguationData":[OSD([sQuery(id+"F19.wireOp",EDGE,"E55.bottom"),sQuery(id+"F19.wireOp",EDGE,"E57")])]});var subQ39=makeQuery(id+"F18.boolean.opBoolean","COPY",FACE,{"disambiguationData":[TD([subQ16])],"derivedFrom":subQ30});var subQ40=sQuery(id+"F15.wireOp",EDGE,"E52.left");var subQ41=makeQuery(id+"F16.boolean.opBoolean","COPY",FACE,{"derivedFrom":makeQuery(id+"F16.opExtrude","CAP_FACE",FACE,{"disambiguationData":[OSD([sQuery(id+"F15.wireOp",EDGE,"E52.bottom"),sQuery(id+"F15.wireOp",EDGE,"E52.top"),subQ40,subQ32])],"isStart":false})});var subQ42=makeQuery(id+"F16.boolean.opBoolean","COPY",FACE,{"derivedFrom":makeQuery(id+"F16.opExtrude","SWEPT_FACE",FACE,{"disambiguationData":[OSD([subQ40])]})});var subQ43=makeQuery(id+"F2.opExtrude","SWEPT_FACE",FACE,{"disambiguationData":[OSD([sQuery(id+"F1.wireOp",EDGE,"E19")])]});var subQ49=subQ20;Q0=makeQuery(id+"F26.boolean.opBoolean","SPLIT",FACE,{"disambiguationData":[TD([subQ35])],"derivedFrom":makeQuery(id+"F24.boolean.opBoolean","MERGE",FACE,{"derivedFrom":[makeQuery(id+"F20.boolean.opBoolean","SPLIT",FACE,{"disambiguationData":[TD([subQ16,subQ15,subQ3,subQ31,subQ39,subQ10,subQ21,subQ38,subQ22])],"derivedFrom":subQ49}),makeQuery(id+"F20.boolean.opBoolean","SPLIT",FACE,{"disambiguationData":[TD([subQ43,subQ37,subQ34,subQ16,subQ2,subQ15,subQ26])],"derivedFrom":subQ49}),makeQuery(id+"F20.boolean.opBoolean","SPLIT",FACE,{"disambiguationData":[TD([subQ35,makeQuery(id+"F2.opExtrude","SWEPT_FACE",FACE,{"disambiguationData":[OSD([sQuery(id+"F1.wireOp",EDGE,"E20")])]}),subQ16,subQ15,subQ3,subQ36,subQ41,subQ42,subQ33,subQ24])],"derivedFrom":subQ49}),subQ11]})});}
            var sketch = newSketch(context, id + "F29", { "sketchPlane" : qUnion([Q0])});
            skLineSegment(sketch, "E74.bottom", {"start": v(-8.22, 46.54) * mm, "end": v(-6.72, 46.54) * mm});
            skLineSegment(sketch, "E74.top", {"start": v(-8.22, 34.54) * mm, "end": v(-6.72, 34.54) * mm});
            skLineSegment(sketch, "E74.left", {"start": v(-8.22, 46.54) * mm, "end": v(-8.22, 34.54) * mm});
            skLineSegment(sketch, "E74.right", {"start": v(-6.72, 46.54) * mm, "end": v(-6.72, 34.54) * mm});
            skSolve(sketch);
        }
        {
            var Q0;
            Q0=qSketchRegion(id+"F29",true);
            extrude(context, id + "F30", {"entities" : qUnion([Q0]), "operationType" : NewBodyOperationType.REMOVE, "endBound" : BoundingType.THROUGH_ALL, "oppositeDirection" : true, "depth" : 25 * mm});
        }
        {
            var Q0;
            {var subQ0=sQuery(id+"F3.wireOp",EDGE,"E22.bottom");Q0=makeQuery(id+"F3.imprint","IMPRINT",FACE,{"disambiguationData":[TD([[makeQuery(id+"F3.imprint","IMPRINT",EDGE,{"derivedFrom":subQ0}),1.0]])]});}
            var Q1;
            Q1=makeQuery(id+"F3.imprint","IMPRINT",FACE,{"disambiguationData":[TD([[makeQuery(id+"F3.imprint","IMPRINT",EDGE,{"derivedFrom":sQuery(id+"F3.wireOp",EDGE,"E25.bottom")}),-1.0]])]});
            var Q2;
            {var subQ0=sQuery(id+"F3.wireOp",EDGE,"E22.bottom");Q2=makeQuery(id+"F3.imprint","IMPRINT",FACE,{"disambiguationData":[TD([[makeQuery(id+"F3.imprint","IMPRINT",EDGE,{"derivedFrom":subQ0}),-1.0]])]});}
            extrude(context, id + "F31", {"entities" : qUnion([Q0, Q1, Q2]), "operationType" : NewBodyOperationType.REMOVE, "endBound" : BoundingType.SYMMETRIC, "oppositeDirection" : true, "depth" : 67.45 * mm});
        }
        {
            var Q0;
            Q0=makeQuery(id+"F2.opExtrude","SWEPT_FACE",FACE,{"disambiguationData":[OSD([sQuery(id+"F1.wireOp",EDGE,"E10.top")])]});
            var sketch = newSketch(context, id + "F32", { "sketchPlane" : qUnion([Q0])});
            skCircle(sketch, "E75", {"center": v(0, -3.3) * mm, "radius": 6.28 * mm});
            skSolve(sketch);
        }
        {
            var Q0;
            Q0=qSketchRegion(id+"F32",true);
            extrude(context, id + "F33", {"entities" : qUnion([Q0]), "operationType" : NewBodyOperationType.REMOVE, "oppositeDirection" : true, "depth" : 2 * mm});
        }
        {
            var Q0;
            {var subQ1=sQuery(id+"F12.wireOp",EDGE,"E39");var subQ2=makeQuery(id+"F14.opExtrude","SWEPT_FACE",FACE,{"disambiguationData":[OSD([subQ1])]});var subQ3=makeQuery(id+"F14.boolean.opBoolean","COPY",FACE,{"derivedFrom":subQ2});var subQ6=sQuery(id+"F17.wireOp",EDGE,"E54.top");var subQ9=makeQuery(id+"F18.opExtrude","SWEPT_FACE",FACE,{"disambiguationData":[OSD([subQ6])]});var subQ10=makeQuery(id+"F18.boolean.opBoolean","COPY",FACE,{"disambiguationData":[TD([subQ3])],"derivedFrom":subQ9});var subQ13=sQuery(id+"F12.wireOp",EDGE,"E40");var subQ14=makeQuery(id+"F13.boolean.opBoolean","COPY",FACE,{"derivedFrom":makeQuery(id+"F13.opExtrude","SWEPT_FACE",FACE,{"disambiguationData":[OSD([subQ13])]})});var subQ15=makeQuery(id+"F14.opExtrude","SWEPT_FACE",FACE,{"disambiguationData":[OSD([subQ13])]});var subQ18=sQuery(id+"F12.wireOp",EDGE,"E51");var subQ19=makeQuery(id+"F14.boolean.opBoolean","COPY",FACE,{"derivedFrom":makeQuery(id+"F14.opExtrude","SWEPT_FACE",FACE,{"disambiguationData":[OSD([subQ18])]})});var subQ20=makeQuery(id+"F18.boolean.opBoolean","COPY",FACE,{"disambiguationData":[TD([subQ14])],"derivedFrom":subQ9});var subQ21=makeQuery(id+"F20.opExtrude","SWEPT_FACE",FACE,{"disambiguationData":[OSD([sQuery(id+"F19.wireOp",EDGE,"E56.bottom"),sQuery(id+"F19.wireOp",EDGE,"E60")])]});var subQ22=makeQuery(id+"F20.opExtrude","SWEPT_FACE",FACE,{"disambiguationData":[OSD([sQuery(id+"F19.wireOp",EDGE,"E56.top"),sQuery(id+"F19.wireOp",EDGE,"E58")])]});var subQ24=makeQuery(id+"F24.opExtrude","SWEPT_FACE",FACE,{"disambiguationData":[OSD([sQuery(id+"F23.wireOp",EDGE,"E64")])]});var subQ27=sQuery(id+"F17.wireOp",EDGE,"E54.bottom");var subQ29=makeQuery(id+"F18.opExtrude","SWEPT_FACE",FACE,{"disambiguationData":[OSD([subQ27])]});var subQ30=makeQuery(id+"F18.boolean.opBoolean","COPY",FACE,{"disambiguationData":[TD([subQ14])],"derivedFrom":subQ29});var subQ31=makeQuery(id+"F20.opExtrude","SWEPT_FACE",FACE,{"disambiguationData":[OSD([sQuery(id+"F19.wireOp",EDGE,"E55.top")])]});var subQ32=sQuery(id+"F15.wireOp",EDGE,"E52.right");var subQ33=makeQuery(id+"F16.boolean.opBoolean","COPY",FACE,{"derivedFrom":makeQuery(id+"F16.opExtrude","SWEPT_FACE",FACE,{"disambiguationData":[OSD([subQ32])]})});var subQ34=makeQuery(id+"F13.boolean.opBoolean","COPY",FACE,{"derivedFrom":makeQuery(id+"F13.opExtrude","SWEPT_FACE",FACE,{"disambiguationData":[OSD([subQ1])]})});var subQ35=makeQuery(id+"F2.opExtrude","SWEPT_FACE",FACE,{"disambiguationData":[OSD([sQuery(id+"F1.wireOp",EDGE,"E10.top")])]});var subQ36=makeQuery(id+"F20.opExtrude","SWEPT_FACE",FACE,{"disambiguationData":[OSD([sQuery(id+"F19.wireOp",EDGE,"E55.bottom"),sQuery(id+"F19.wireOp",EDGE,"E57")])]});var subQ37=makeQuery(id+"F18.boolean.opBoolean","COPY",FACE,{"disambiguationData":[TD([subQ3])],"derivedFrom":subQ29});var subQ38=makeQuery(id+"F2.opExtrude","SWEPT_FACE",FACE,{"disambiguationData":[OSD([sQuery(id+"F1.wireOp",EDGE,"E19")])]});var subQ43=sQuery(id+"F15.wireOp",EDGE,"E52.left");var subQ44=makeQuery(id+"F16.boolean.opBoolean","COPY",FACE,{"derivedFrom":makeQuery(id+"F16.opExtrude","CAP_FACE",FACE,{"disambiguationData":[OSD([sQuery(id+"F15.wireOp",EDGE,"E52.bottom"),sQuery(id+"F15.wireOp",EDGE,"E52.top"),subQ43,subQ32])],"isStart":false})});var subQ45=makeQuery(id+"F13.boolean.opBoolean","COPY",FACE,{"derivedFrom":makeQuery(id+"F13.opExtrude","CAP_FACE",FACE,{"disambiguationData":[OSD([sQuery(id+"F1.wireOp",EDGE,"E6.bottom"),sQuery(id+"F8.wireOp",EDGE,"E28"),sQuery(id+"F12.wireOp",EDGE,"E33"),sQuery(id+"F12.wireOp",EDGE,"E34.top"),sQuery(id+"F12.wireOp",EDGE,"E34.left"),sQuery(id+"F12.wireOp",EDGE,"E34.right"),sQuery(id+"F12.wireOp",EDGE,"E35"),sQuery(id+"F12.wireOp",EDGE,"E36"),sQuery(id+"F12.wireOp",EDGE,"E37"),sQuery(id+"F12.wireOp",EDGE,"E38"),subQ1,subQ13,sQuery(id+"F12.wireOp",EDGE,"E44"),subQ18])],"isStart":false})});var subQ46=makeQuery(id+"F14.boolean.opBoolean","COPY",FACE,{"derivedFrom":subQ15});var subQ47=makeQuery(id+"F16.boolean.opBoolean","COPY",FACE,{"derivedFrom":makeQuery(id+"F16.opExtrude","SWEPT_FACE",FACE,{"disambiguationData":[OSD([subQ43])]})});var subQ49=subQ19;Q0=makeQuery(id+"F26.boolean.opBoolean","SPLIT",FACE,{"disambiguationData":[TD([subQ35])],"derivedFrom":makeQuery(id+"F24.boolean.opBoolean","MERGE",FACE,{"derivedFrom":[makeQuery(id+"F20.boolean.opBoolean","SPLIT",FACE,{"disambiguationData":[TD([subQ14,subQ15,subQ3,subQ37,subQ30,subQ10,subQ20,subQ36,subQ21])],"derivedFrom":subQ49}),makeQuery(id+"F20.boolean.opBoolean","SPLIT",FACE,{"disambiguationData":[TD([subQ38,subQ45,subQ34,subQ14,subQ2,subQ15,subQ31])],"derivedFrom":subQ49}),makeQuery(id+"F20.boolean.opBoolean","SPLIT",FACE,{"disambiguationData":[TD([subQ35,makeQuery(id+"F2.opExtrude","SWEPT_FACE",FACE,{"disambiguationData":[OSD([sQuery(id+"F1.wireOp",EDGE,"E20")])]}),subQ14,subQ15,subQ3,subQ46,subQ44,subQ47,subQ33,subQ22])],"derivedFrom":subQ49}),subQ24]})});}
            var sketch = newSketch(context, id + "F34", { "sketchPlane" : qUnion([Q0])});
            skLineSegment(sketch, "E76.bottom", {"start": v(-7.5, 33.67) * mm, "end": v(-4.38, 33.67) * mm});
            skLineSegment(sketch, "E76.top", {"start": v(-7.5, 30.83) * mm, "end": v(-4.38, 30.83) * mm});
            skLineSegment(sketch, "E76.left", {"start": v(-7.5, 33.67) * mm, "end": v(-7.5, 33.24) * mm});
            skLineSegment(sketch, "E76.right", {"start": v(-4.38, 33.67) * mm, "end": v(-4.38, 32.96) * mm});
            skArc(sketch, "E77", {"start": v(-5.02, 30.94) * mm, "mid": v(-6.25, 31.33) * mm, "end": v(-7.5, 31) * mm});
            skLineSegment(sketch, "E78", {"start": v(-6.28, 31.33) * mm, "end": v(-6.28, 31.33) * mm});
            skLineSegment(sketch, "E79", {"start": v(-6.28, 31.33) * mm, "end": v(-4.35, 32.95) * mm});
            skLineSegment(sketch, "E80", {"start": v(-7.5, 31) * mm, "end": v(-7.5, 33.24) * mm});
            skArc(sketch, "E81", {"start": v(-4.35, 32.95) * mm, "mid": v(-5.9, 33.38) * mm, "end": v(-7.5, 33.24) * mm});
            skLineSegment(sketch, "E82", {"start": v(-4.18, 29.98) * mm, "end": v(-2.37, 31) * mm});
            skLineSegment(sketch, "E83", {"start": v(-4.31, 27.72) * mm, "end": v(-4.31, 27.72) * mm});
            skLineSegment(sketch, "E84", {"start": v(-2.25, 27.2) * mm, "end": v(-2.25, 27.2) * mm});
            skLineSegment(sketch, "E85", {"start": v(-7.5, 31) * mm, "end": v(-7.5, 31) * mm});
            skArc(sketch, "E86", {"start": v(-4.31, 27.72) * mm, "mid": v(-4.62, 30.61) * mm, "end": v(-7.5, 31) * mm});
            skArc(sketch, "E87", {"start": v(-7.5, 31) * mm, "mid": v(-8, 27.33) * mm, "end": v(-4.31, 27.72) * mm});
            skArc(sketch, "E88", {"start": v(-4.18, 29.98) * mm, "mid": v(-4.53, 30.52) * mm, "end": v(-5.02, 30.94) * mm});
            skLineSegment(sketch, "E89", {"start": v(-4.31, 27.72) * mm, "end": v(-2.25, 27.2) * mm});
            skArc(sketch, "E90", {"start": v(-2.25, 27.2) * mm, "mid": v(-1.88, 29.11) * mm, "end": v(-2.37, 31) * mm});
            skArc(sketch, "E91", {"start": v(-2.37, 31) * mm, "mid": v(-4.54, 33.03) * mm, "end": v(-7.5, 33.24) * mm});
            skLineSegment(sketch, "E92", {"start": v(-4.38, 32.96) * mm, "end": v(-4.38, 32.96) * mm});
            skLineSegment(sketch, "E93", {"start": v(-7.5, 33.24) * mm, "end": v(-7.5, 30.83) * mm});
            skArc(sketch, "E94", {"start": v(-6.28, 31.33) * mm, "mid": v(-7.58, 26.99) * mm, "end": v(-4.18, 29.98) * mm});
            skLineSegment(sketch, "E95", {"start": v(-4.38, 32.96) * mm, "end": v(-4.38, 30.83) * mm});
            skSolve(sketch);
        }
        {
            var Q0;
            {var subQ14=sQuery(id+"F34.wireOp",EDGE,"E76.bottom");Q0=makeQuery(id+"F34.imprint","IMPRINT",FACE,{"disambiguationData":[TD([[makeQuery(id+"F34.imprint","IMPRINT",EDGE,{"derivedFrom":subQ14}),-1.0]])]});}
            var Q1;
            {var subQ0=sQuery(id+"F34.wireOp",EDGE,"E95");var subQ1=sQuery(id+"F34.wireOp",EDGE,"E79");var subQ2=makeQuery(id+"F34.imprint","INTERSECT",VERTEX,{"derivedFrom":[subQ1,subQ0]});Q1=makeQuery(id+"F34.imprint","IMPRINT",FACE,{"disambiguationData":[TD([[makeQuery(id+"F34.imprint","IMPRINT",EDGE,{"disambiguationData":[TD([[subQ2,1.0]])],"derivedFrom":subQ1}),-1.0]])]});}
            var Q2;
            {var subQ1=sQuery(id+"F34.wireOp",EDGE,"E86");Q2=makeQuery(id+"F34.imprint","IMPRINT",FACE,{"disambiguationData":[TD([[makeQuery(id+"F34.imprint","IMPRINT",EDGE,{"derivedFrom":subQ1}),-1.0]])]});}
            var Q3;
            {var subQ1=sQuery(id+"F34.wireOp",EDGE,"E86");Q3=makeQuery(id+"F34.imprint","IMPRINT",FACE,{"disambiguationData":[TD([[makeQuery(id+"F34.imprint","IMPRINT",EDGE,{"derivedFrom":subQ1}),1.0]])]});}
            var Q4;
            {var subQ0=sQuery(id+"F34.wireOp",EDGE,"E76.right");var subQ12=sQuery(id+"F34.wireOp",EDGE,"E91");var subQ13=makeQuery(id+"F34.imprint","INTERSECT",VERTEX,{"derivedFrom":[subQ0,subQ12,sQuery(id+"F34.wireOp",EDGE,"E95")]});Q4=makeQuery(id+"F34.imprint","IMPRINT",FACE,{"disambiguationData":[TD([[makeQuery(id+"F34.imprint","IMPRINT",EDGE,{"disambiguationData":[TD([[subQ13,1.0]])],"derivedFrom":subQ0}),-1.0]])]});}
            var Q5;
            {var subQ7=makeQuery(id+"F14.boolean.opBoolean","COPY",FACE,{"derivedFrom":makeQuery(id+"F14.opExtrude","SWEPT_FACE",FACE,{"disambiguationData":[OSD([sQuery(id+"F12.wireOp",EDGE,"E39")])]})});var subQ8=sQuery(id+"F17.wireOp",EDGE,"E53.right");var subQ9=sQuery(id+"F17.wireOp",EDGE,"E53.top");var subQ11=makeQuery(id+"F18.opExtrude","SWEPT_FACE",FACE,{"disambiguationData":[OSD([subQ8]),TDD([makeQuery(id+"F17.imprint","IMPRINT",EDGE,{"disambiguationData":[TD([[makeQuery(id+"F17.imprint","INTERSECT",VERTEX,{"derivedFrom":[subQ9,subQ8]}),1.0]])],"derivedFrom":subQ8})])]});var subQ15=sQuery(id+"F12.wireOp",EDGE,"E40");var subQ18=makeQuery(id+"F13.boolean.opBoolean","COPY",FACE,{"derivedFrom":makeQuery(id+"F13.opExtrude","SWEPT_FACE",FACE,{"disambiguationData":[OSD([subQ15])]})});Q5=makeQuery(id+"F24.boolean.opBoolean","SPLIT",FACE,{"disambiguationData":[TD([subQ7])],"derivedFrom":makeQuery(id+"F20.boolean.opBoolean","MERGE",FACE,{"derivedFrom":[makeQuery(id+"F18.boolean.opBoolean","COPY",FACE,{"disambiguationData":[TD([subQ7])],"derivedFrom":subQ11}),makeQuery(id+"F18.boolean.opBoolean","COPY",FACE,{"disambiguationData":[TD([subQ18])],"derivedFrom":subQ11}),makeQuery(id+"F20.opExtrude","SWEPT_FACE",FACE,{"disambiguationData":[OSD([sQuery(id+"F19.wireOp",EDGE,"E56.right")])]})]})});}
            extrude(context, id + "F35", {"entities" : qUnion([Q0, Q1, Q2, Q3, Q4]), "operationType" : NewBodyOperationType.REMOVE, "endBound" : BoundingType.UP_TO_SURFACE, "endBoundEntityFace" : qUnion([Q5]), "depth" : 25 * mm});
        }
        {
            var Q0;
            {var subQ0=sQuery(id+"F34.wireOp",EDGE,"E82");Q0=makeQuery(id+"F34.imprint","IMPRINT",FACE,{"disambiguationData":[TD([[makeQuery(id+"F34.imprint","IMPRINT",EDGE,{"derivedFrom":subQ0}),-1.0]])]});}
            var Q1;
            {var subQ7=makeQuery(id+"F14.boolean.opBoolean","COPY",FACE,{"derivedFrom":makeQuery(id+"F14.opExtrude","SWEPT_FACE",FACE,{"disambiguationData":[OSD([sQuery(id+"F12.wireOp",EDGE,"E39")])]})});var subQ8=sQuery(id+"F17.wireOp",EDGE,"E53.right");var subQ9=sQuery(id+"F17.wireOp",EDGE,"E53.top");var subQ11=makeQuery(id+"F18.opExtrude","SWEPT_FACE",FACE,{"disambiguationData":[OSD([subQ8]),TDD([makeQuery(id+"F17.imprint","IMPRINT",EDGE,{"disambiguationData":[TD([[makeQuery(id+"F17.imprint","INTERSECT",VERTEX,{"derivedFrom":[subQ9,subQ8]}),1.0]])],"derivedFrom":subQ8})])]});var subQ15=sQuery(id+"F12.wireOp",EDGE,"E40");var subQ18=makeQuery(id+"F13.boolean.opBoolean","COPY",FACE,{"derivedFrom":makeQuery(id+"F13.opExtrude","SWEPT_FACE",FACE,{"disambiguationData":[OSD([subQ15])]})});Q1=makeQuery(id+"F24.boolean.opBoolean","SPLIT",FACE,{"disambiguationData":[TD([subQ7])],"derivedFrom":makeQuery(id+"F20.boolean.opBoolean","MERGE",FACE,{"derivedFrom":[makeQuery(id+"F18.boolean.opBoolean","COPY",FACE,{"disambiguationData":[TD([subQ7])],"derivedFrom":subQ11}),makeQuery(id+"F18.boolean.opBoolean","COPY",FACE,{"disambiguationData":[TD([subQ18])],"derivedFrom":subQ11}),makeQuery(id+"F20.opExtrude","SWEPT_FACE",FACE,{"disambiguationData":[OSD([sQuery(id+"F19.wireOp",EDGE,"E56.right")])]})]})});}
            extrude(context, id + "F36", {"entities" : qUnion([Q0]), "operationType" : NewBodyOperationType.ADD, "endBound" : BoundingType.UP_TO_SURFACE, "endBoundEntityFace" : qUnion([Q1]), "depth" : 25 * mm});
        }
        {
            var Q0;
            Q0=makeQuery(id+"F2.opExtrude","SWEPT_FACE",FACE,{"disambiguationData":[OSD([sQuery(id+"F1.wireOp",EDGE,"E10.top")])]});
            var sketch = newSketch(context, id + "F37", { "sketchPlane" : qUnion([Q0])});
            skLineSegment(sketch, "E96", {"start": v(-9.7, -3.3) * mm, "end": v(-9.25, -12.55) * mm});
            skLineSegment(sketch, "E97", {"start": v(-8.25, -13.5) * mm, "end": v(8.25, -13.5) * mm});
            skLineSegment(sketch, "E98", {"start": v(9.25, -12.55) * mm, "end": v(9.7, -3.3) * mm});
            skLineSegment(sketch, "E99", {"start": v(-9.7, -3.3) * mm, "end": v(9.7, -3.3) * mm});
            skPoint(sketch, "E100.visualSharp", {"position": v(-9.2, -13.5) * mm});
            skArc(sketch, "E100.filletArc", {"start": v(-9.25, -12.55) * mm, "mid": v(-8.94, -13.22) * mm, "end": v(-8.25, -13.5) * mm});
            skPoint(sketch, "E101.visualSharp", {"position": v(9.2, -13.5) * mm});
            skArc(sketch, "E101.filletArc", {"start": v(8.25, -13.5) * mm, "mid": v(8.94, -13.22) * mm, "end": v(9.25, -12.55) * mm});
            skLineSegment(sketch, "E102", {"start": v(-9.7, -3.3) * mm, "end": v(-9.7, -13.5) * mm});
            skLineSegment(sketch, "E103", {"start": v(-9.7, -13.5) * mm, "end": v(9.7, -13.5) * mm});
            skLineSegment(sketch, "E104", {"start": v(9.7, -13.5) * mm, "end": v(9.7, -3.3) * mm});
            skSolve(sketch);
        }
        {
            var Q0;
            Q0=makeQuery(id+"F37.imprint","IMPRINT",FACE,{"disambiguationData":[TD([[makeQuery(id+"F37.imprint","IMPRINT",EDGE,{"derivedFrom":sQuery(id+"F37.wireOp",EDGE,"E96")}),-1.0]])]});
            var Q1;
            Q1=makeQuery(id+"F37.imprint","IMPRINT",FACE,{"disambiguationData":[TD([[makeQuery(id+"F37.imprint","IMPRINT",EDGE,{"derivedFrom":sQuery(id+"F37.wireOp",EDGE,"E98")}),-1.0]])]});
            extrude(context, id + "F38", {"entities" : qUnion([Q0, Q1]), "operationType" : NewBodyOperationType.REMOVE, "endBound" : BoundingType.THROUGH_ALL, "oppositeDirection" : true, "depth" : 25 * mm});
        }
    });
